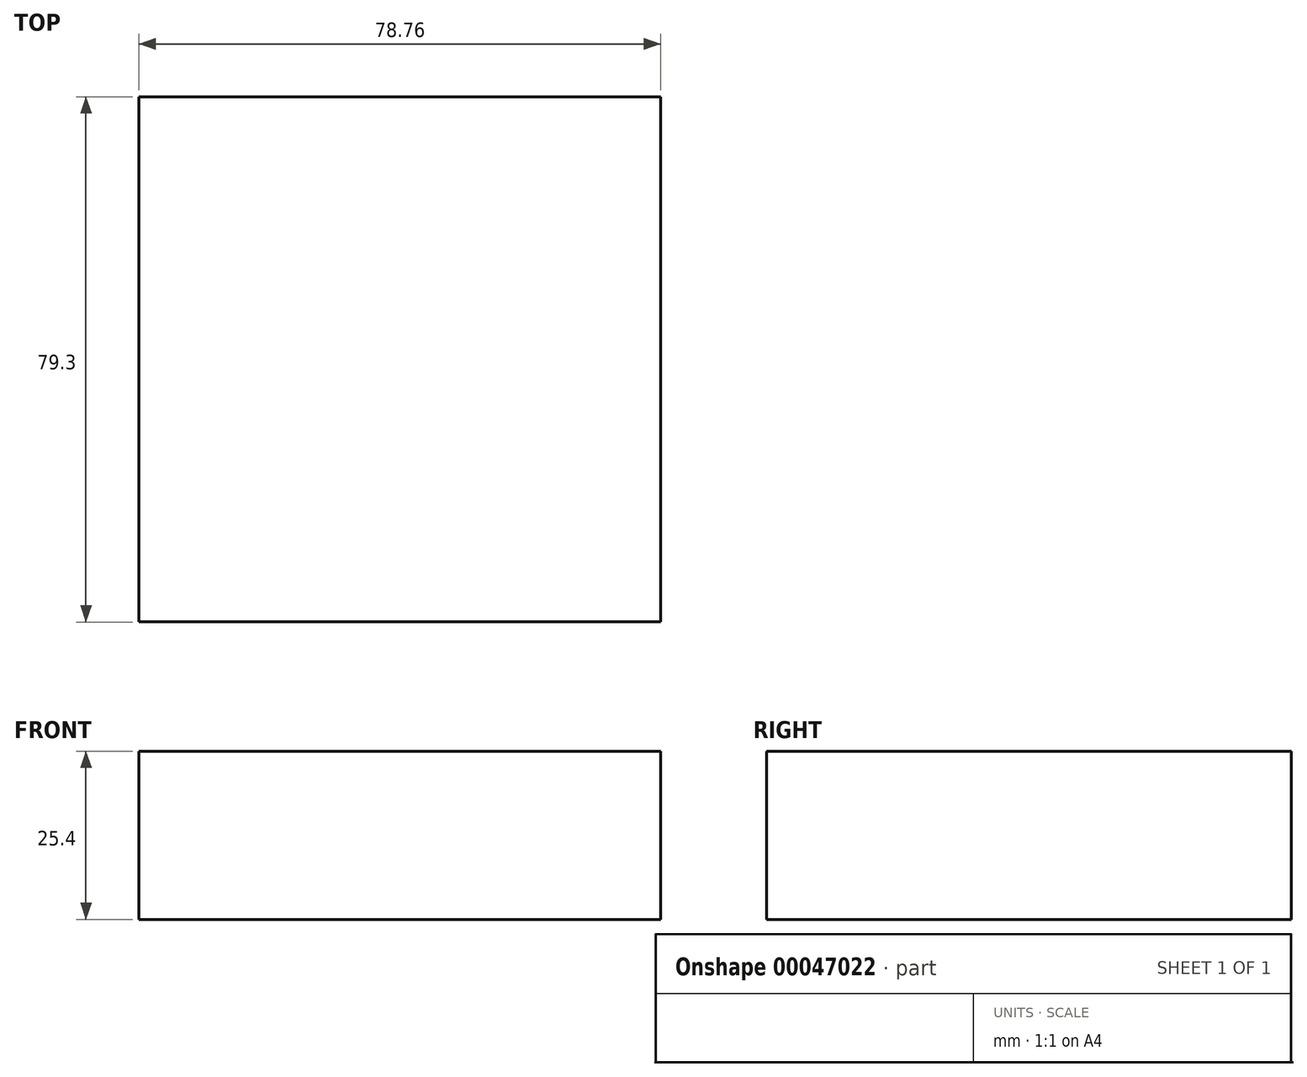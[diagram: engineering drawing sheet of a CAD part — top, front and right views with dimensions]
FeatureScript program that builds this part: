
annotation { "Feature Type Name" : "Feature", "Feature Type Description" : "" }
export const myFeature = defineFeature(function(context is Context, id is Id, definition is map)
    precondition{}
    {
        {
            var Q0;
            Q0=qCreatedBy(makeId("Top.planeOp"),FACE);
            var sketch = newSketch(context, id + "F0", { "sketchPlane" : qUnion([Q0])});
            skLineSegment(sketch, "E0.rect.bottom", {"start": v(39.38, -39.65) * mm, "end": v(-39.38, -39.65) * mm});
            skLineSegment(sketch, "E0.rect.top", {"start": v(39.38, 39.65) * mm, "end": v(-39.38, 39.65) * mm});
            skLineSegment(sketch, "E0.rect.left", {"start": v(39.38, -39.65) * mm, "end": v(39.38, 39.65) * mm});
            skLineSegment(sketch, "E0.rect.right", {"start": v(-39.38, -39.65) * mm, "end": v(-39.38, 39.65) * mm});
            skPoint(sketch, "E0.rect.middle", {"position": v(0, 0) * mm});
            skSolve(sketch);
        }
        {
            var Q0;
            Q0=makeQuery(id+"F0.imprint","IMPRINT",FACE,{"disambiguationData":[TD([[makeQuery(id+"F0.imprint","IMPRINT",EDGE,{"derivedFrom":sQuery(id+"F0.wireOp",EDGE,"E0.rect.bottom")}),-1.0]])]});
            extrude(context, id + "F1", {"entities" : qUnion([Q0]), "depth" : 25.4 * mm});
        }
    });
